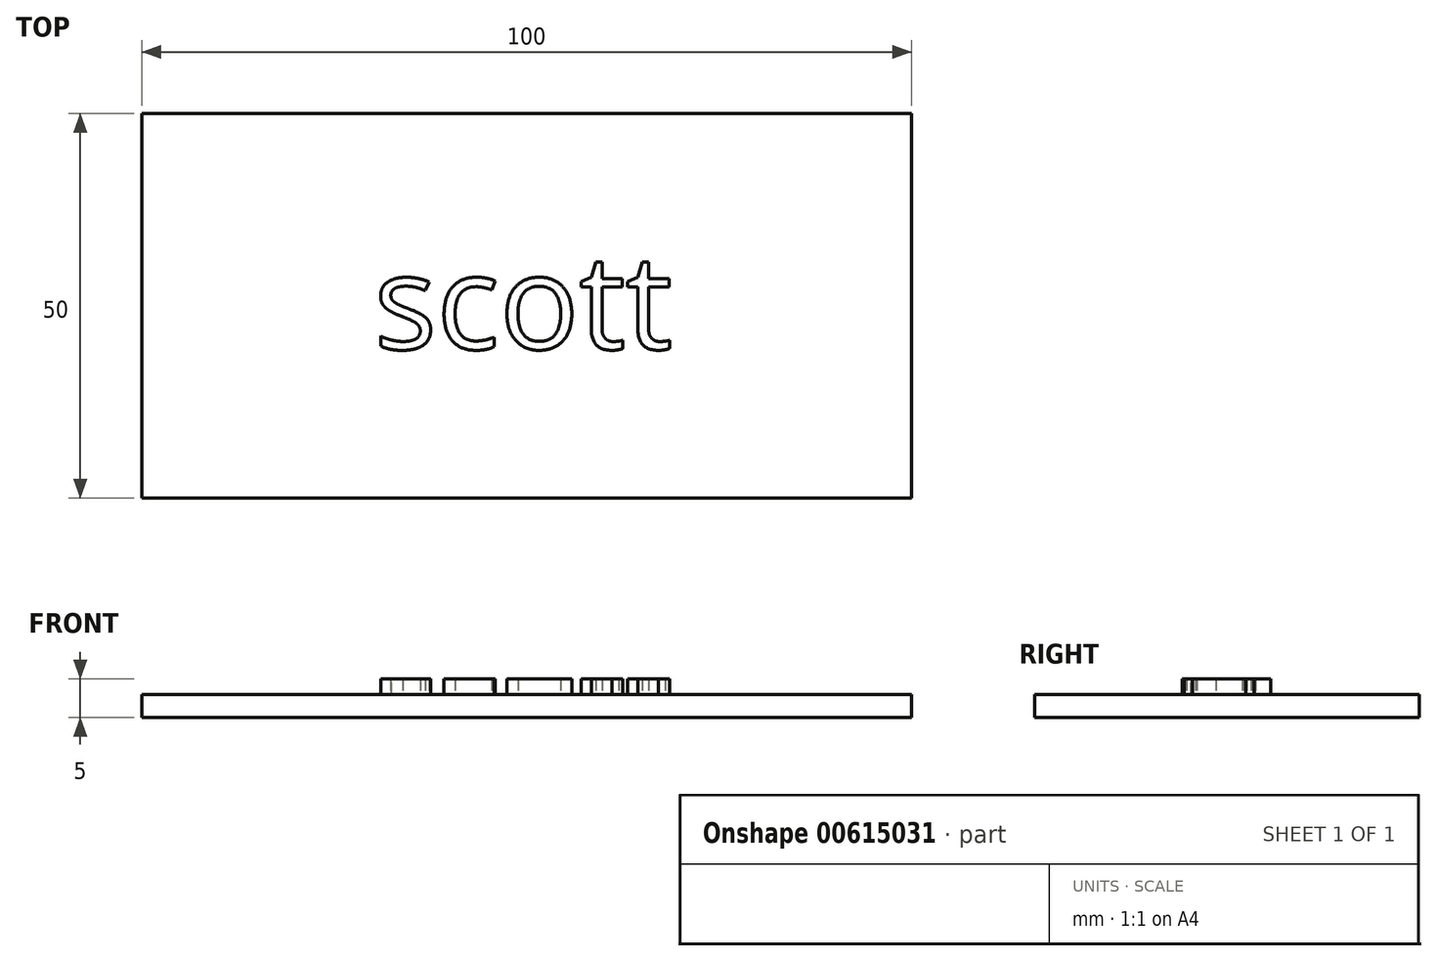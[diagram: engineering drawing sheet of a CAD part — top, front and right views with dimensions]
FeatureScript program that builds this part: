
annotation { "Feature Type Name" : "Feature", "Feature Type Description" : "" }
export const myFeature = defineFeature(function(context is Context, id is Id, definition is map)
    precondition{}
    {
        {
            var Q0;
            Q0=qCreatedBy(makeId("Top.planeOp"),FACE);
            var sketch = newSketch(context, id + "F0", { "sketchPlane" : qUnion([Q0])});
            skLineSegment(sketch, "E0.bottom", {"start": v(0, 0) * mm, "end": v(100, 0) * mm});
            skLineSegment(sketch, "E0.top", {"start": v(0, 50) * mm, "end": v(100, 50) * mm});
            skLineSegment(sketch, "E0.left", {"start": v(0, 0) * mm, "end": v(0, 50) * mm});
            skLineSegment(sketch, "E0.right", {"start": v(100, 0) * mm, "end": v(100, 50) * mm});
            skSolve(sketch);
        }
        {
            var Q0;
            Q0=makeQuery(id+"F0.imprint","IMPRINT",FACE,{"disambiguationData":[TD([[makeQuery(id+"F0.imprint","IMPRINT",EDGE,{"derivedFrom":sQuery(id+"F0.wireOp",EDGE,"E0.bottom")}),1.0]])]});
            extrude(context, id + "F1", {"entities" : qUnion([Q0]), "depth" : 3 * mm, "offsetDistance" : 25 * mm});
        }
        {
            var Q0;
            Q0=makeQuery(id+"F1.opExtrude","CAP_FACE",FACE,{"disambiguationData":[OSD([sQuery(id+"F0.wireOp",EDGE,"E0.bottom"),sQuery(id+"F0.wireOp",EDGE,"E0.top"),sQuery(id+"F0.wireOp",EDGE,"E0.left"),sQuery(id+"F0.wireOp",EDGE,"E0.right")])],"isStart":false});
            var sketch = newSketch(context, id + "F2", { "sketchPlane" : qUnion([Q0])});
            skPoint(sketch, "E1.firstSnap0", {"position": v(0, 25) * mm});
            skText(sketch, "E2", { "text": "scott", "fontName": "OpenSans-Regular.ttf"});
            const initialGuessF2  = {"E2": [0.03013, 0.01937, 1, 0, 0.01234]};
            skSetInitialGuess(sketch, initialGuessF2);
            skSolve(sketch);
        }
        {
            var Q0;
            Q0 = qSketchRegion(id + "F2", true);
            extrude(context, id + "F3", {"entities" : qUnion([Q0]), "operationType" : NewBodyOperationType.ADD, "depth" : 2 * mm, "offsetDistance" : 25 * mm});
        }
    });
